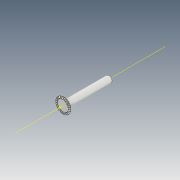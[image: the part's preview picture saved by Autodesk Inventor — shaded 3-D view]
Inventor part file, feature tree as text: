
AUTODESK INVENTOR PART (.ipt)
format: ipt  version: 2021 (Build 250183000, 183)  size: 505,344 bytes
history: native  units: mm
features: other x16, sketch x10, loft x3, pattern_circular x3, extrude x1
ambient origin geometry x6: Origin, XZ Plane, X Axis, Y Axis, Z Axis, Center Point
bodies: Solid1 (feature_tree)
feature tree (33):
  other  "Ponto superior"
  other  "Plano de malha 2"
  other  "Corpo dentado"
  other  "Ponto inicial"
  other  "Plano de dente"
  sketch  "Esboço inicial"  dims[d3=0.6mm]
  other  "Extremidade"
  loft  "Loft"
  pattern_circular  "Circular Pattern"  [2 undecoded]
  sketch  "Esboço 3D direito"  dims[d4=1.194087mm]
  other  "Plano final direito"
  loft  "Transição direita"
  pattern_circular  "Padrão circular direito"  Angle=90.0deg  [1 undecoded]
  sketch  "Esboço 3D esquerdo"  dims[d5=90.0deg]
  other  "Plano final esquerdo"
  loft  "Transição esquerda"
  pattern_circular  "Padrão circular esquerdo"  Angle=360.0deg  [1 undecoded]
  other  "Fixar corpo"
  extrude  "Extrusão1"  Depth=10.0mm
  other  "Plano de malha"
  other  "Plano superior"
  sketch  "Esboço de corpo dentado"  dims[d7=1.663639mm]
  other  "Plano final"
  sketch  "Esboço final"  dims[d8=1.691227mm]
  other  "Helical Curve Left"
  sketch  "Esboço final esquerdo"  dims[d9=4.071779mm]
  sketch  "Esboço de corpo"  dims[d11=0.6198mm]
  sketch  "Sketch6"  dims[d0=4.68mm d1=4.46412mm]
  other  "Srf1"
  other  "Helical Curve Right"
  sketch  "Esboço final direita"  dims[d12=1.281954mm d15=1.303212mm d16=3.137599mm d17=0.0mm d18=90.0deg d19=0.0mm d20=90.0deg d21=260.0mm d22=360.0deg d26=17.944705mm d27=0.309728mm d28=4.68mm d29=-10.47518mm d30=1.281954mm d31=1.303212mm d32=3.137599mm d35=0.0mm d37=0.0mm d39=0.0mm d40=90.0deg d41=260.0mm d42=360.0deg d46=90.0deg d47=90.0deg d48=0.0mm d49=0.0mm d50=90.0deg d51=1.208305mm d52=0.0mm d53=0.0mm d54=0.0mm d56=0.94732mm d57=4.981399mm d58=4.419079mm d59=3.838526mm d60=3.405218mm d61=3.838526mm d62=3.405218mm d65=17.944705mm d66=31.5mm d67=4.68mm d68=-10.47518mm d69=0.309728mm d70=1.303212mm d71=3.137599mm d72=1.281954mm d73=3.405218mm d74=3.838526mm d75=0.0mm d77=0.0mm d79=0.0mm d80=90.0deg d81=260.0mm d82=360.0deg d84=10.0mm d85=20.0mm d86=20.0mm d87=10.0mm d88=0.0mm d89=0.0mm d90=90.0deg d91=90.0deg d92=90.0deg d93=90.0deg d94=14.5mm d95=0.0mm]
  sketch  "Esboço8"  dims[d2=4.8599mm]
  other  "Diâmetro do flanco"
note: 4 required parameter values undecoded (feature->parameter linkage not recoverable at this tier; creation-order binding heuristic only, values carry confidence <= 0.55)
